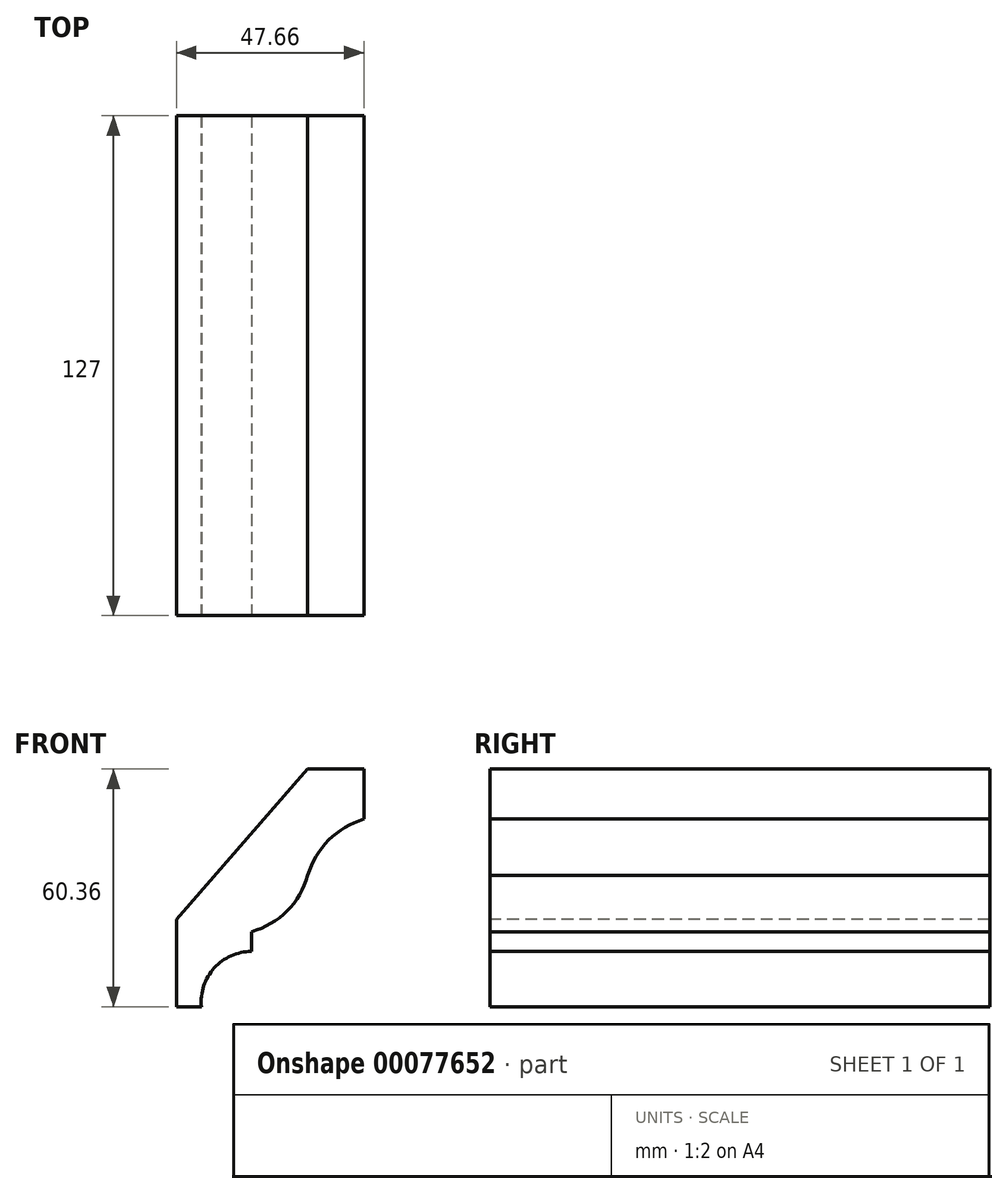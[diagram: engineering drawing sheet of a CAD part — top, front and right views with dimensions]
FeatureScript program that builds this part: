
annotation { "Feature Type Name" : "Feature", "Feature Type Description" : "" }
export const myFeature = defineFeature(function(context is Context, id is Id, definition is map)
    precondition{}
    {
        {
            var Q0;
            Q0=qCreatedBy(makeId("Front.planeOp"),FACE);
            var sketch = newSketch(context, id + "F0", { "sketchPlane" : qUnion([Q0])});
            skLineSegment(sketch, "E0", {"start": v(23.83, 30.18) * mm, "end": v(23.83, 17.47) * mm});
            skLineSegment(sketch, "E1", {"start": v(-23.83, -30.18) * mm, "end": v(-17.47, -30.18) * mm});
            skLineSegment(sketch, "E2", {"start": v(-23.83, -30.18) * mm, "end": v(-23.83, -7.94) * mm});
            skLineSegment(sketch, "E3", {"start": v(-23.83, -7.94) * mm, "end": v(9.46, 30.18) * mm});
            skLineSegment(sketch, "E4", {"start": v(-4.77, -16.23) * mm, "end": v(-4.77, -11.12) * mm});
            skArc(sketch, "E5", {"start": v(-4.77, -16.16) * mm, "mid": v(-14.23, -20.36) * mm, "end": v(-17.47, -30.18) * mm});
            skArc(sketch, "E6", {"start": v(-4.77, -11.12) * mm, "mid": v(4.3, -5.88) * mm, "end": v(9.53, 3.18) * mm});
            skArc(sketch, "E7", {"start": v(23.83, 17.47) * mm, "mid": v(14.87, 12.14) * mm, "end": v(9.53, 3.18) * mm});
            skLineSegment(sketch, "E8", {"start": v(9.46, 30.18) * mm, "end": v(23.83, 30.18) * mm});
            skSolve(sketch);
        }
        {
            var Q0;
            Q0=makeQuery(id+"F0.imprint","IMPRINT",FACE,{"disambiguationData":[TD([[makeQuery(id+"F0.imprint","IMPRINT",EDGE,{"derivedFrom":sQuery(id+"F0.wireOp",EDGE,"E1")}),1.0]])]});
            extrude(context, id + "F1", {"entities" : qUnion([Q0]), "oppositeDirection" : true, "depth" : 127 * mm});
        }
    });
